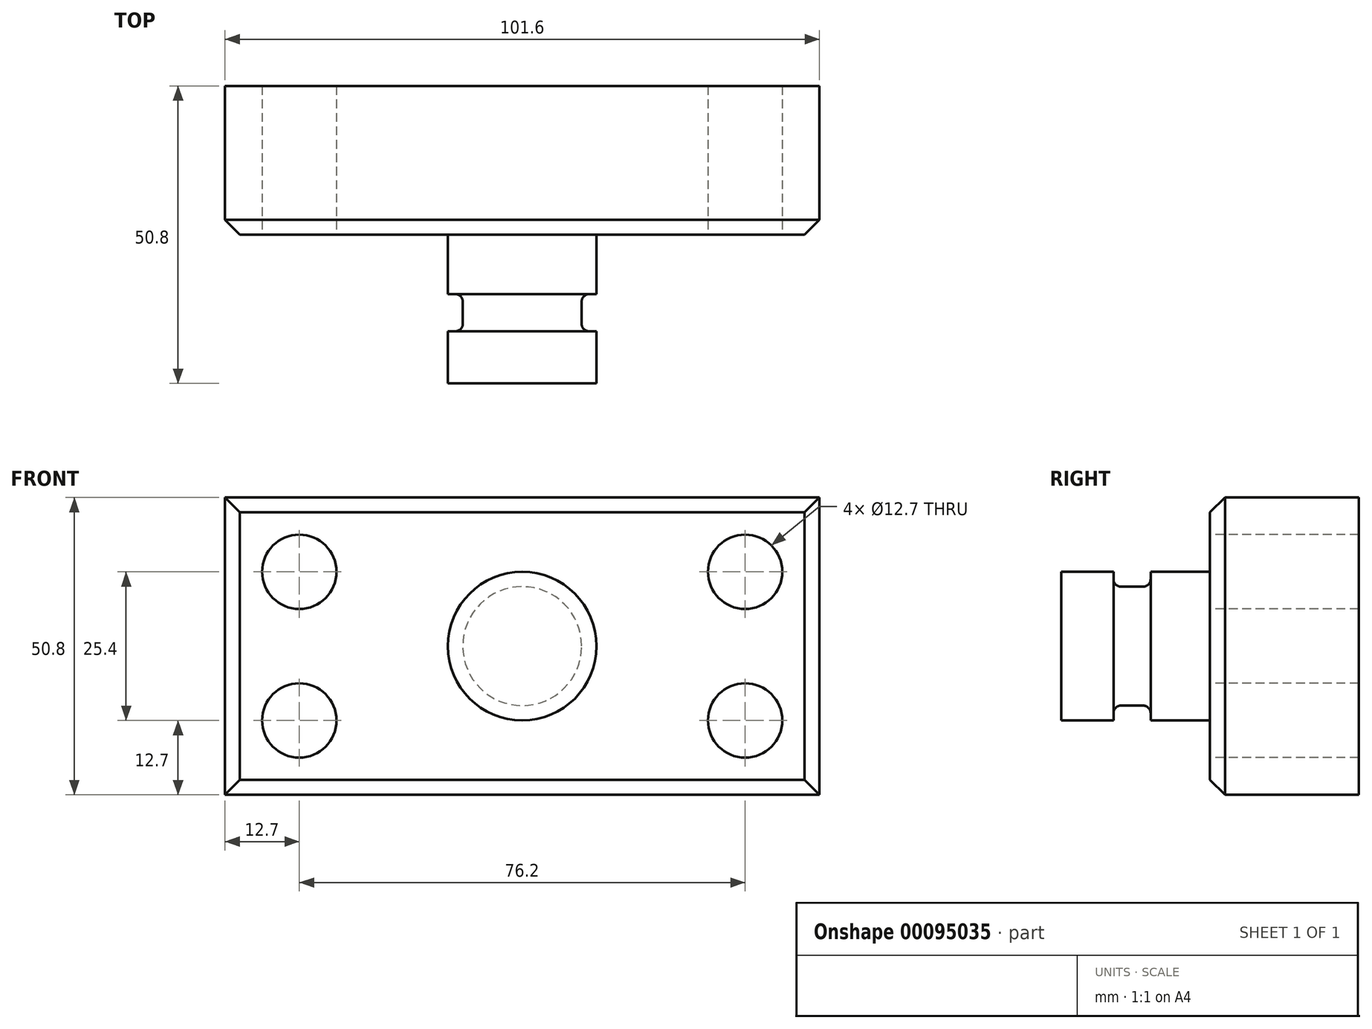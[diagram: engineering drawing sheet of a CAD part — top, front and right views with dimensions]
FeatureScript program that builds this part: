
annotation { "Feature Type Name" : "Feature", "Feature Type Description" : "" }
export const myFeature = defineFeature(function(context is Context, id is Id, definition is map)
    precondition{}
    {
        {
            var Q0;
            Q0=qCreatedBy(makeId("Front.planeOp"),FACE);
            var sketch = newSketch(context, id + "F0", { "sketchPlane" : qUnion([Q0])});
            skLineSegment(sketch, "E0.bottom", {"start": v(50.8, 25.4) * mm, "end": v(-50.8, 25.4) * mm});
            skLineSegment(sketch, "E0.top", {"start": v(50.8, -25.4) * mm, "end": v(-50.8, -25.4) * mm});
            skLineSegment(sketch, "E0.left", {"start": v(50.8, 25.4) * mm, "end": v(50.8, -25.4) * mm});
            skLineSegment(sketch, "E0.right", {"start": v(-50.8, 25.4) * mm, "end": v(-50.8, -25.4) * mm});
            skPoint(sketch, "E0.middle", {"position": v(0, 0) * mm});
            skSolve(sketch);
        }
        {
            var Q0;
            Q0 = qSketchRegion(id + "F0", true);
            extrude(context, id + "F1", {"entities" : qUnion([Q0]), "depth" : 25.4 * mm});
        }
        {
            var Q0;
            Q0=makeQuery(id+"F1.opExtrude","CAP_FACE",FACE,{"disambiguationData":[OSD([sQuery(id+"F0.wireOp",EDGE,"E0.bottom"),sQuery(id+"F0.wireOp",EDGE,"E0.top"),sQuery(id+"F0.wireOp",EDGE,"E0.left"),sQuery(id+"F0.wireOp",EDGE,"E0.right")])],"isStart":false});
            var sketch = newSketch(context, id + "F2", { "sketchPlane" : qUnion([Q0])});
            skCircle(sketch, "E1", {"center": v(-38.1, 12.7) * mm, "radius": 6.35 * mm});
            skCircle(sketch, "E2", {"center": v(-38.1, -12.7) * mm, "radius": 6.35 * mm});
            skCircle(sketch, "E3", {"center": v(38.1, 12.7) * mm, "radius": 6.35 * mm});
            skCircle(sketch, "E4", {"center": v(38.1, -12.7) * mm, "radius": 6.35 * mm});
            skSolve(sketch);
        }
        {
            var Q0;
            Q0 = qSketchRegion(id + "F2", true);
            extrude(context, id + "F3", {"entities" : qUnion([Q0]), "operationType" : NewBodyOperationType.REMOVE, "endBound" : BoundingType.THROUGH_ALL, "oppositeDirection" : true, "depth" : 25.4 * mm});
        }
        {
            var Q0;
            Q0=qCreatedBy(makeId("Top.planeOp"),FACE);
            var sketch = newSketch(context, id + "F4", { "sketchPlane" : qUnion([Q0])});
            skLineSegment(sketch, "E5.bottom", {"start": v(0, -25.4) * mm, "end": v(-12.7, -25.4) * mm});
            skLineSegment(sketch, "E5.top", {"start": v(0, -50.8) * mm, "end": v(-12.7, -50.8) * mm});
            skLineSegment(sketch, "E5.left", {"start": v(0, -25.4) * mm, "end": v(0, -50.8) * mm});
            skLineSegment(sketch, "E5.right", {"start": v(-12.7, -25.4) * mm, "end": v(-12.7, -50.8) * mm});
            skSolve(sketch);
        }
        {
            var Q0;
            Q0=makeQuery(id+"F4.imprint","IMPRINT",FACE,{"disambiguationData":[TD([[makeQuery(id+"F4.imprint","IMPRINT",EDGE,{"derivedFrom":sQuery(id+"F4.wireOp",EDGE,"E5.bottom")}),1.0]])]});
            var Q1;
            Q1=sQuery(id+"F4.wireOp",EDGE,"E5.left");
            revolve(context, id + "F5", {"operationType" : NewBodyOperationType.ADD, "entities" : qUnion([Q0]), "axis" : qUnion([Q1]), "revolveType" : RevolveType.FULL});
        }
        {
            var Q0;
            Q0=qCreatedBy(makeId("Top.planeOp"),FACE);
            var sketch = newSketch(context, id + "F6", { "sketchPlane" : qUnion([Q0])});
            skLineSegment(sketch, "E6.bottom", {"start": v(-18.31, -41.9) * mm, "end": v(-10.16, -41.9) * mm});
            skLineSegment(sketch, "E6.top", {"start": v(-18.31, -35.56) * mm, "end": v(-10.16, -35.56) * mm});
            skLineSegment(sketch, "E6.left", {"start": v(-18.31, -41.91) * mm, "end": v(-18.31, -35.56) * mm});
            skLineSegment(sketch, "E6.right", {"start": v(-10.16, -41.9) * mm, "end": v(-10.16, -35.56) * mm});
            skLineSegment(sketch, "E7", {"start": v(0, 0) * mm, "end": v(0, -76.54) * mm, "construction": true});
            skSolve(sketch);
        }
        {
            var Q0;
            Q0=makeQuery(id+"F6.imprint","IMPRINT",FACE,{"disambiguationData":[TD([[makeQuery(id+"F6.imprint","IMPRINT",EDGE,{"derivedFrom":sQuery(id+"F6.wireOp",EDGE,"E6.bottom")}),1.0]])]});
            var Q1;
            Q1=sQuery(id+"F6.wireOp",EDGE,"E7");
            revolve(context, id + "F7", {"operationType" : NewBodyOperationType.REMOVE, "entities" : qUnion([Q0]), "axis" : qUnion([Q1]), "revolveType" : RevolveType.FULL, "oppositeDirection" : true});
        }
        {
            var Q0;
            Q0=makeQuery(id+"F5.opRevolve","SWEPT_EDGE",EDGE,{"disambiguationData":[OSD([sQuery(id+"F4.wireOp",EDGE,"E5.bottom"),sQuery(id+"F4.wireOp",EDGE,"E5.right")])]});
            var Q1;
            Q1=makeQuery(id+"F7.boolean.opBoolean","COPY",EDGE,{"derivedFrom":makeQuery(id+"F7.opRevolve","SWEPT_EDGE",EDGE,{"disambiguationData":[OSD([sQuery(id+"F6.wireOp",EDGE,"E6.bottom"),sQuery(id+"F6.wireOp",EDGE,"E6.right")])]})});
            var Q2;
            Q2=makeQuery(id+"F7.boolean.opBoolean","COPY",EDGE,{"derivedFrom":makeQuery(id+"F7.opRevolve","SWEPT_EDGE",EDGE,{"disambiguationData":[OSD([sQuery(id+"F6.wireOp",EDGE,"E6.top"),sQuery(id+"F6.wireOp",EDGE,"E6.right")])]})});
            fillet(context, id + "F8", {"entities" : qUnion([Q0, Q1, Q2]), "radius" : 1.27 * mm, "tangentPropagation" : true, "allowEdgeOverflow" : false});
        }
        {
            var Q0;
            Q0=makeQuery(id+"F1.opExtrude","CAP_EDGE",EDGE,{"disambiguationData":[OSD([sQuery(id+"F0.wireOp",EDGE,"E0.top")])],"isStart":false});
            var Q1;
            Q1=makeQuery(id+"F1.opExtrude","CAP_EDGE",EDGE,{"disambiguationData":[OSD([sQuery(id+"F0.wireOp",EDGE,"E0.left")])],"isStart":false});
            var Q2;
            Q2=makeQuery(id+"F1.opExtrude","CAP_EDGE",EDGE,{"disambiguationData":[OSD([sQuery(id+"F0.wireOp",EDGE,"E0.right")])],"isStart":false});
            var Q3;
            Q3=makeQuery(id+"F1.opExtrude","CAP_EDGE",EDGE,{"disambiguationData":[OSD([sQuery(id+"F0.wireOp",EDGE,"E0.bottom")])],"isStart":false});
            chamfer(context, id + "F9", {"entities" : qUnion([Q0, Q1, Q2, Q3]), "width" : 2.54 * mm, "tangentPropagation" : true});
        }
    });
